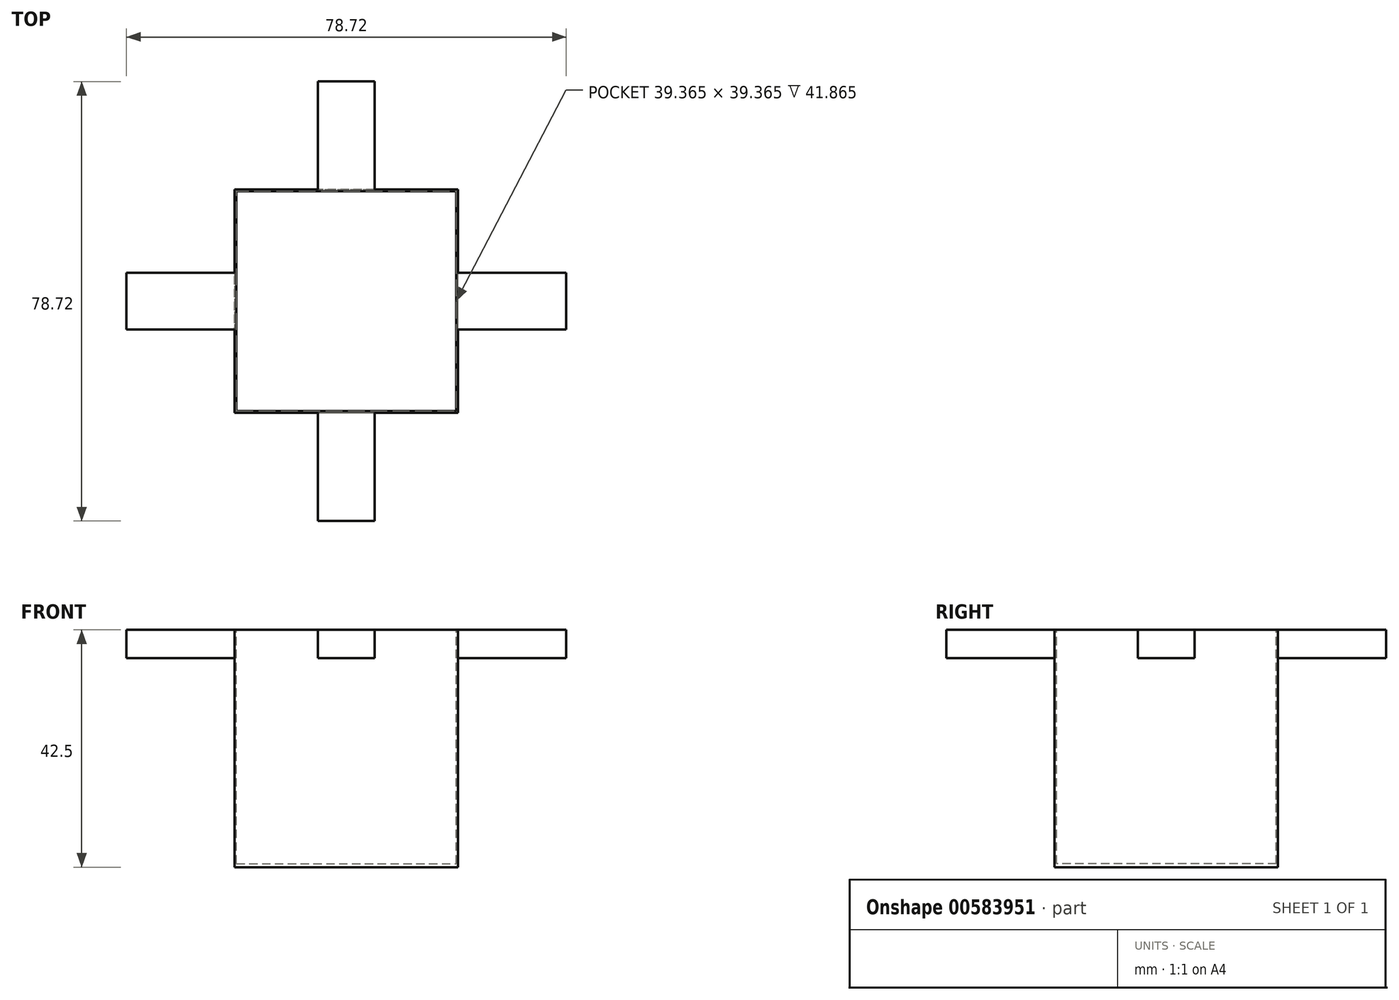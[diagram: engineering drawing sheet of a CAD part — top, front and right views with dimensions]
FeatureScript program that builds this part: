
annotation { "Feature Type Name" : "Feature", "Feature Type Description" : "" }
export const myFeature = defineFeature(function(context is Context, id is Id, definition is map)
    precondition{}
    {
        {
            var Q0;
            Q0=qCreatedBy(makeId("Front.planeOp"),FACE);
            var sketch = newSketch(context, id + "F0", { "sketchPlane" : qUnion([Q0])});
            skLineSegment(sketch, "E0.bottom", {"start": v(-20, 21.25) * mm, "end": v(20, 21.25) * mm});
            skLineSegment(sketch, "E0.top", {"start": v(-20, -21.25) * mm, "end": v(20, -21.25) * mm});
            skLineSegment(sketch, "E0.left", {"start": v(-20, 21.25) * mm, "end": v(-20, -21.25) * mm});
            skLineSegment(sketch, "E0.right", {"start": v(20, 21.25) * mm, "end": v(20, -21.25) * mm});
            skPoint(sketch, "E0.middle", {"position": v(0, 0) * mm});
            skSolve(sketch);
        }
        {
            var Q0;
            Q0=makeQuery(id+"F0.imprint","IMPRINT",FACE,{"disambiguationData":[TD([[makeQuery(id+"F0.imprint","IMPRINT",EDGE,{"derivedFrom":sQuery(id+"F0.wireOp",EDGE,"E0.bottom")}),-1.0]])]});
            extrude(context, id + "F1", {"entities" : qUnion([Q0]), "endBound" : BoundingType.SYMMETRIC, "depth" : 40 * mm, "offsetDistance" : 25.4 * mm});
        }
        {
            var Q0;
            Q0=makeQuery(id+"F1.opExtrude","SWEPT_FACE",FACE,{"disambiguationData":[OSD([sQuery(id+"F0.wireOp",EDGE,"E0.bottom")])]});
            var sketch = newSketch(context, id + "F2", { "sketchPlane" : qUnion([Q0])});
            skLineSegment(sketch, "E1.bottom", {"start": v(-19.68, 19.68) * mm, "end": v(19.68, 19.68) * mm});
            skLineSegment(sketch, "E1.top", {"start": v(-19.68, -19.68) * mm, "end": v(19.68, -19.68) * mm});
            skLineSegment(sketch, "E1.left", {"start": v(-19.68, 19.68) * mm, "end": v(-19.68, -19.68) * mm});
            skLineSegment(sketch, "E1.right", {"start": v(19.68, 19.68) * mm, "end": v(19.68, -19.68) * mm});
            skPoint(sketch, "E1.middle", {"position": v(0, 0) * mm});
            skSolve(sketch);
        }
        {
            var Q0;
            Q0=makeQuery(id+"F2.imprint","IMPRINT",FACE,{"disambiguationData":[TD([[makeQuery(id+"F2.imprint","IMPRINT",EDGE,{"derivedFrom":sQuery(id+"F2.wireOp",EDGE,"E1.bottom")}),-1.0]])]});
            extrude(context, id + "F3", {"entities" : qUnion([Q0]), "operationType" : NewBodyOperationType.REMOVE, "oppositeDirection" : true, "depth" : 41.86 * mm, "offsetDistance" : 25.4 * mm});
        }
        {
            var Q0;
            Q0=makeQuery(id+"F1.opExtrude","CAP_FACE",FACE,{"disambiguationData":[OSD([sQuery(id+"F0.wireOp",EDGE,"E0.bottom"),sQuery(id+"F0.wireOp",EDGE,"E0.top"),sQuery(id+"F0.wireOp",EDGE,"E0.left"),sQuery(id+"F0.wireOp",EDGE,"E0.right")])],"isStart":false});
            var sketch = newSketch(context, id + "F4", { "sketchPlane" : qUnion([Q0])});
            skLineSegment(sketch, "E2.bottom", {"start": v(-5.08, 26.33) * mm, "end": v(5.08, 26.33) * mm});
            skLineSegment(sketch, "E2.top", {"start": v(-5.08, 16.17) * mm, "end": v(5.08, 16.17) * mm});
            skLineSegment(sketch, "E2.left", {"start": v(-5.08, 26.33) * mm, "end": v(-5.08, 16.17) * mm});
            skLineSegment(sketch, "E2.right", {"start": v(5.08, 26.33) * mm, "end": v(5.08, 16.17) * mm});
            skPoint(sketch, "E2.middle", {"position": v(0, 21.25) * mm});
            skSolve(sketch);
        }
        {
            var Q0;
            Q0=makeQuery(id+"F1.opExtrude","SWEPT_FACE",FACE,{"disambiguationData":[OSD([sQuery(id+"F0.wireOp",EDGE,"E0.left")])]});
            var sketch = newSketch(context, id + "F5", { "sketchPlane" : qUnion([Q0])});
            skLineSegment(sketch, "E3.bottom", {"start": v(-5.08, 26.33) * mm, "end": v(5.08, 26.33) * mm});
            skLineSegment(sketch, "E3.top", {"start": v(-5.08, 16.17) * mm, "end": v(5.08, 16.17) * mm});
            skLineSegment(sketch, "E3.left", {"start": v(-5.08, 26.33) * mm, "end": v(-5.08, 16.17) * mm});
            skLineSegment(sketch, "E3.right", {"start": v(5.08, 26.33) * mm, "end": v(5.08, 16.17) * mm});
            skPoint(sketch, "E3.middle", {"position": v(0, 21.25) * mm});
            skSolve(sketch);
        }
        {
            var Q0;
            Q0=makeQuery(id+"F1.opExtrude","CAP_FACE",FACE,{"disambiguationData":[OSD([sQuery(id+"F0.wireOp",EDGE,"E0.bottom"),sQuery(id+"F0.wireOp",EDGE,"E0.top"),sQuery(id+"F0.wireOp",EDGE,"E0.left"),sQuery(id+"F0.wireOp",EDGE,"E0.right")])],"isStart":true});
            var sketch = newSketch(context, id + "F6", { "sketchPlane" : qUnion([Q0])});
            skLineSegment(sketch, "E4.bottom", {"start": v(-5.08, 26.33) * mm, "end": v(5.08, 26.33) * mm});
            skLineSegment(sketch, "E4.top", {"start": v(-5.08, 16.17) * mm, "end": v(5.08, 16.17) * mm});
            skLineSegment(sketch, "E4.left", {"start": v(-5.08, 26.33) * mm, "end": v(-5.08, 16.17) * mm});
            skLineSegment(sketch, "E4.right", {"start": v(5.08, 26.33) * mm, "end": v(5.08, 16.17) * mm});
            skPoint(sketch, "E4.middle", {"position": v(0, 21.25) * mm});
            skSolve(sketch);
        }
        {
            var Q0;
            Q0=makeQuery(id+"F1.opExtrude","SWEPT_FACE",FACE,{"disambiguationData":[OSD([sQuery(id+"F0.wireOp",EDGE,"E0.right")])]});
            var sketch = newSketch(context, id + "F7", { "sketchPlane" : qUnion([Q0])});
            skLineSegment(sketch, "E5.bottom", {"start": v(-5.08, 26.33) * mm, "end": v(5.08, 26.33) * mm});
            skLineSegment(sketch, "E5.top", {"start": v(-5.08, 16.17) * mm, "end": v(5.08, 16.17) * mm});
            skLineSegment(sketch, "E5.left", {"start": v(-5.08, 26.33) * mm, "end": v(-5.08, 16.17) * mm});
            skLineSegment(sketch, "E5.right", {"start": v(5.08, 26.33) * mm, "end": v(5.08, 16.17) * mm});
            skPoint(sketch, "E5.middle", {"position": v(0, 21.25) * mm});
            skSolve(sketch);
        }
        {
            var Q0;
            {var subQ0=sQuery(id+"F4.wireOp",EDGE,"E2.top");Q0=makeQuery(id+"F4.imprint","IMPRINT",FACE,{"disambiguationData":[TD([[makeQuery(id+"F4.imprint","IMPRINT",EDGE,{"derivedFrom":subQ0}),1.0]])]});}
            extrude(context, id + "F8", {"entities" : qUnion([Q0]), "operationType" : NewBodyOperationType.ADD, "depth" : 19.37 * mm, "offsetDistance" : 25.4 * mm});
        }
        {
            var Q0;
            {var subQ0=sQuery(id+"F5.wireOp",EDGE,"E3.top");Q0=makeQuery(id+"F5.imprint","IMPRINT",FACE,{"disambiguationData":[TD([[makeQuery(id+"F5.imprint","IMPRINT",EDGE,{"derivedFrom":subQ0}),1.0]])]});}
            extrude(context, id + "F9", {"entities" : qUnion([Q0]), "operationType" : NewBodyOperationType.ADD, "depth" : 19.37 * mm, "offsetDistance" : 25.4 * mm});
        }
        {
            var Q0;
            {var subQ0=sQuery(id+"F6.wireOp",EDGE,"E4.top");Q0=makeQuery(id+"F6.imprint","IMPRINT",FACE,{"disambiguationData":[TD([[makeQuery(id+"F6.imprint","IMPRINT",EDGE,{"derivedFrom":subQ0}),1.0]])]});}
            extrude(context, id + "F10", {"entities" : qUnion([Q0]), "operationType" : NewBodyOperationType.ADD, "depth" : 19.37 * mm, "offsetDistance" : 25.4 * mm});
        }
        {
            var Q0;
            {var subQ0=sQuery(id+"F7.wireOp",EDGE,"E5.top");Q0=makeQuery(id+"F7.imprint","IMPRINT",FACE,{"disambiguationData":[TD([[makeQuery(id+"F7.imprint","IMPRINT",EDGE,{"derivedFrom":subQ0}),1.0]])]});}
            extrude(context, id + "F11", {"entities" : qUnion([Q0]), "operationType" : NewBodyOperationType.ADD, "depth" : 19.37 * mm, "offsetDistance" : 25.4 * mm});
        }
    });
